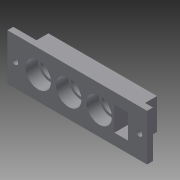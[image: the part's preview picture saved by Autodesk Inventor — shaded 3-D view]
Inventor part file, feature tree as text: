
AUTODESK INVENTOR PART (.ipt)
format: ipt  version: 2014 SP1 (Build 180222100, 222)  size: 203,264 bytes
history: native  units: in
note: dims shown in document units (in); Inventor stores cm internally (conversion verified against a paired STEP export)
features: extrude x11, sketch x10
ambient origin geometry x8: Origin, YZ Plane, XZ Plane, XY Plane, X Axis, Y Axis, Z Axis, Center Point
bodies: Solid1 (feature_tree)
feature tree (21):
  extrude  "Extrusion1"  Depth=0.5in
  extrude  "Extrusion2"  Depth=0.0938in TaperAngle=0.0deg
  extrude  "Extrusion3"  Depth=0.057in
  extrude  "Extrusion5"  Depth=0.39in TaperAngle=0.0deg
  extrude  "Extrusion8"  Depth=0.0938in
  extrude  "Extrusion9"  Depth=0.0938in
  extrude  "Extrusion10"  Depth=0.325in
  extrude  "Extrusion11"  Depth=0.41in TaperAngle=0.0deg
  extrude  "Extrusion12"  Depth=0.325in
  extrude  "Extrusion15"  Depth=0.5in TaperAngle=0.0deg
  extrude  "Extrusion16"  Depth=0.5in TaperAngle=0.0deg
  sketch  "Sketch1"  dims[d0=1.75in d1=0.5in]
  sketch  "Sketch2"  dims[d2=0.5in d3=0.0in d4=0.0938in d5=0.0in]
  sketch  "Sketch5"  dims[d13=0.22in d14=0.057in]
  sketch  "Sketch8"  dims[d16=0.39in d17=0.4375in d18=0.0in]
  sketch  "Sketch9"  dims[d25=0.0938in d26=0.0938in]
  sketch  "Sketch10"  dims[d27=0.0938in d28=0.0in d47=0.325in]
  sketch  "Sketch11"  dims[d48=0.325in d49=0.325in]
  sketch  "Sketch12"  dims[d53=0.41in d54=0.4375in d55=0.0in]
  sketch  "Sketch15"  dims[d56=0.325in d57=0.325in]
  sketch  "Sketch16"  dims[d58=0.325in d59=0.5in d60=0.0in d61=0.5in d62=0.0in d63=0.325in d73=0.3in d74=0.0in d75=0.375in d76=0.0in d77=0.41in d78=0.41in d95=0.055in d100=0.09in d101=0.0in d102=1.0in d103=0.0in]
